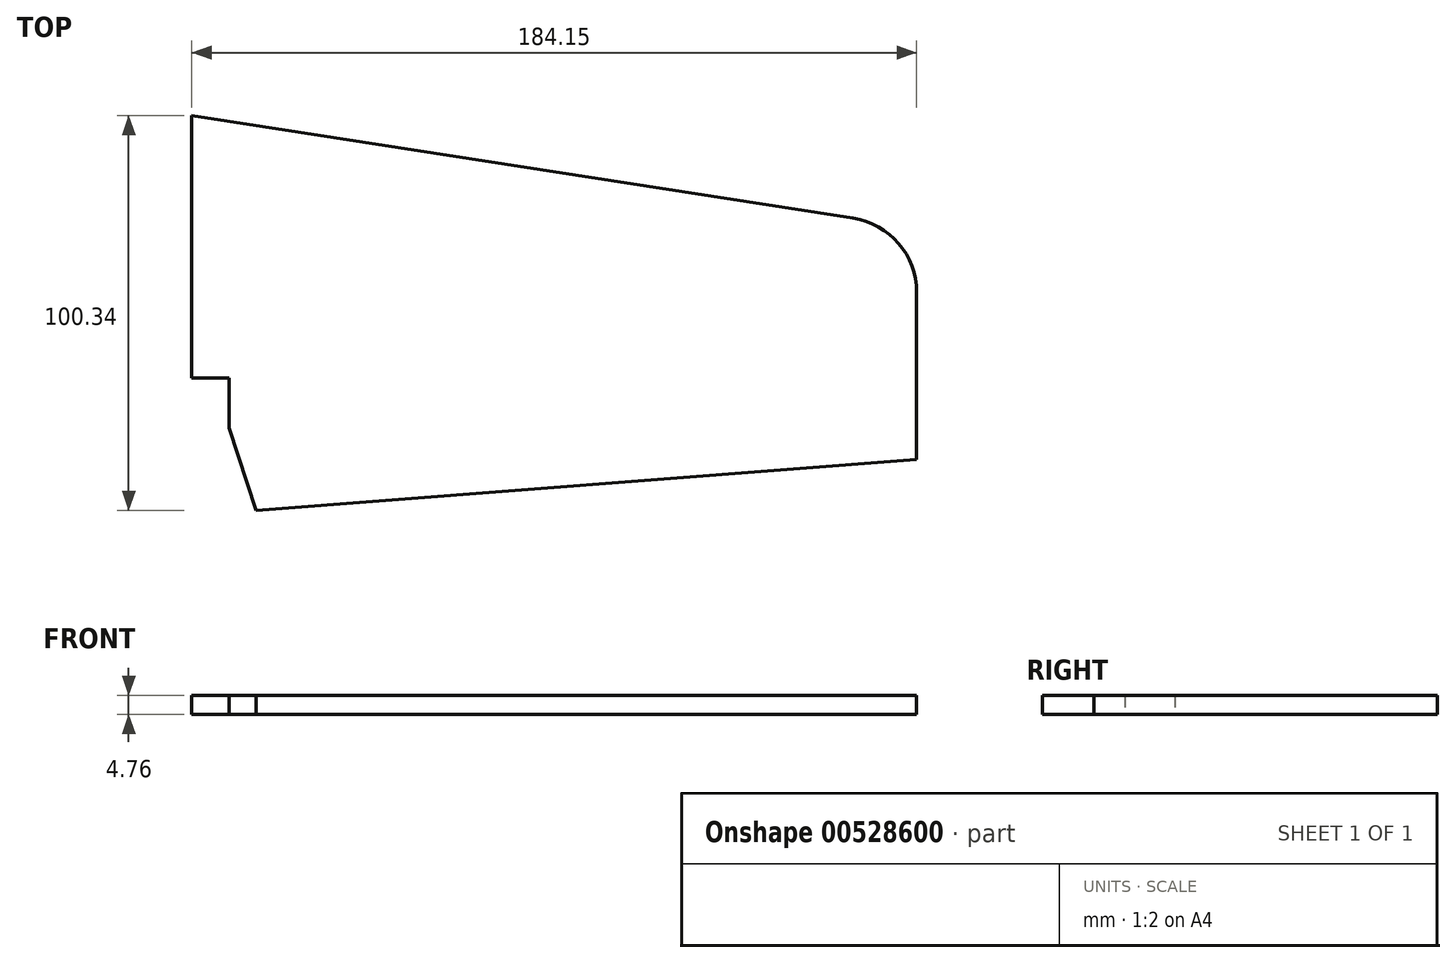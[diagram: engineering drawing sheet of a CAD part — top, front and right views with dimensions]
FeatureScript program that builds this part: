
annotation { "Feature Type Name" : "Feature", "Feature Type Description" : "" }
export const myFeature = defineFeature(function(context is Context, id is Id, definition is map)
    precondition{}
    {
        {
            var Q0;
            Q0=qCreatedBy(makeId("Top.planeOp"),FACE);
            var sketch = newSketch(context, id + "F0", { "sketchPlane" : qUnion([Q0])});
            skLineSegment(sketch, "E0", {"start": v(0, 101.6) * mm, "end": v(0, 0) * mm});
            skLineSegment(sketch, "E1", {"start": v(184.15, 56.7) * mm, "end": v(184.15, 14.29) * mm});
            skLineSegment(sketch, "E2", {"start": v(0, 101.6) * mm, "end": v(168.02, 75.53) * mm});
            skLineSegment(sketch, "E3", {"start": v(184.15, 14.29) * mm, "end": v(184.15, 34.93) * mm});
            skLineSegment(sketch, "E4", {"start": v(184.15, 73.03) * mm, "end": v(0, 73.02) * mm, "construction": true});
            skLineSegment(sketch, "E5", {"start": v(184.15, 14.29) * mm, "end": v(16.3, 1.26) * mm});
            skLineSegment(sketch, "E6", {"start": v(0, 101.6) * mm, "end": v(210.45, 101.6) * mm, "construction": true});
            skLineSegment(sketch, "E7", {"start": v(184.15, 73.03) * mm, "end": v(184.15, 101.6) * mm, "construction": true});
            skPoint(sketch, "E8.visualSharp", {"position": v(184.15, 73.03) * mm});
            skArc(sketch, "E8.filletArc", {"start": v(184.15, 56.7) * mm, "mid": v(179.57, 69.1) * mm, "end": v(168.02, 75.53) * mm});
            skPoint(sketch, "E9.orphan", {"position": v(9.52, 34.93) * mm});
            skLineSegment(sketch, "E10", {"start": v(9.52, 34.93) * mm, "end": v(9.52, 22.23) * mm});
            skLineSegment(sketch, "E11", {"start": v(9.52, 22.23) * mm, "end": v(16.3, 1.26) * mm});
            skLineSegment(sketch, "E12", {"start": v(0, 34.93) * mm, "end": v(9.52, 34.93) * mm});
            skSolve(sketch);
        }
        {
            var Q0;
            Q0=makeQuery(id+"F0.imprint","IMPRINT",FACE,{"disambiguationData":[TD([[makeQuery(id+"F0.imprint","IMPRINT",EDGE,{"derivedFrom":sQuery(id+"F0.wireOp",EDGE,"E0")}),1.0]])]});
            extrude(context, id + "F1", {"entities" : qUnion([Q0]), "depth" : 4.76 * mm, "offsetDistance" : 25.4 * mm});
        }
    });
